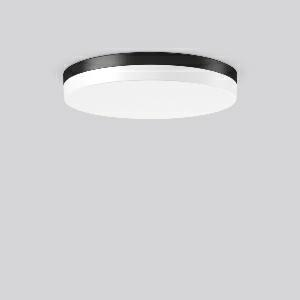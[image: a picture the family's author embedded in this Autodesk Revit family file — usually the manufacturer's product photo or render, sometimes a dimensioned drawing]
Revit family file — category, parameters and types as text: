
# Revit family: flat_slim_round_312677_0031_19_42d7
name_source: partatom
category: Lighting Fixtures
units: mm (PartAtom-declared; Revit-internal decimal feet)

## family parameters
Cut with Voids When Loaded = No
Host = Face
Light Source = No
Part Type = Normal
Room Calculation Point = No
Round Connector Dimension = Use Diameter
Shared = No

## types (1)
- MultiLumen 1 830 (1 x LED Modul 830, 3350 lm, 3000)
    Apparent Load = 31 VA
    CIE Flux Codes = 41 71 90 86 100
    Color Rendering = 80
    Color Temperature = 3000
    Default Elevation = 1800 mm
    Height = 75 mm
    Lamp = 1 x LED Modul 830
    Lamp Light Flux = 3350 lm
    Lamp count = 1
    Length = 480 mm
    Lifetime = 50000 h
    Luminous efficacy = 108 lm/W
    Manufacturer = RZB
    ModVariant = No
    Model = 312677.0031.19
    Mounting Place = Ceiling
    Mounting Type = Surface mounted
    Number of Poles = 1
    OnlyDefault = Yes
    Power Factor = 1
    Product Name = FLAT SLIM round
    Product group = Surface mounted ceiling and wall luminaires
    ProductGroupID = 305
    Protection Class = Protection class I
    Protection Degree = Degree of protection
    RLX_Detail_Level = 1
    RLX_Emergency_Light_Flux = 0 lm
    RLX_Emergency_Type = 0
    RLX_Emergency_Type_DB = No
    RlxData = <blob elided: 23365 chars, md5=8bccc6ed>
    Socket = socket
    Standby Power = 0 W
    System Light Flux = 3350 lm
    System Power = 31 W
    Type Comments = MultiLumen 1 830
    Type Image = 312633.0031.jpg
    URL = http://relux.com
    VarID = multilumen_1_830
    Voltage = 0 V
    Weight = 0.00 kg
    Width = 0 mm  [stored 0 ft]

note: [stored X ft] marks values corroborated as IEEE doubles in the binary element streams (Revit-internal decimal feet)

## geometry (parser evidence)
native form markers: Blend x4, Sweep x13
no freeform markers — native parametric forms only
